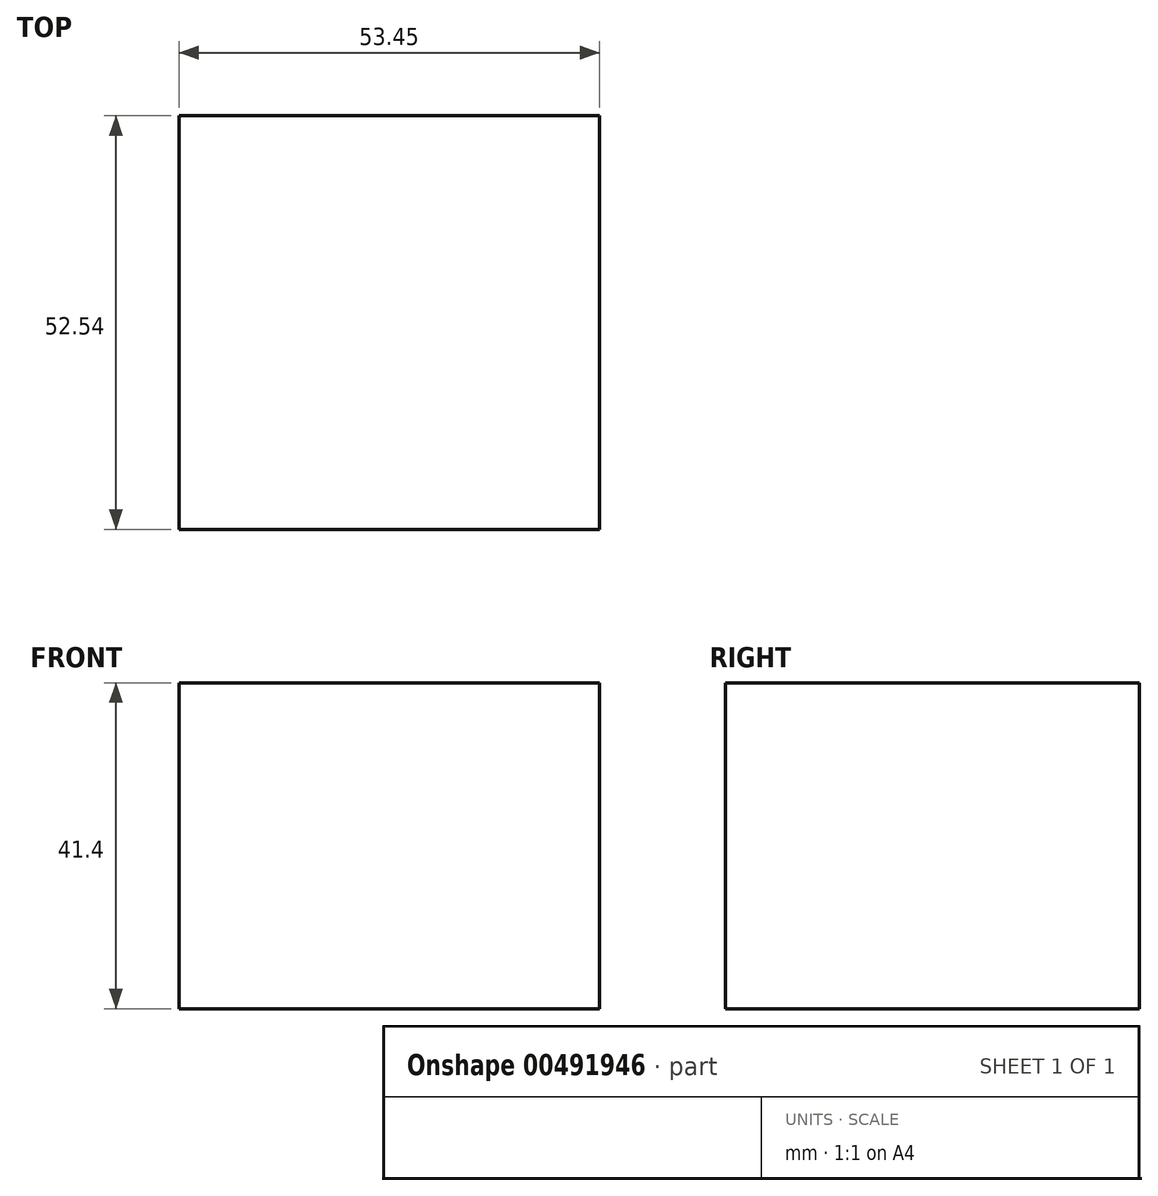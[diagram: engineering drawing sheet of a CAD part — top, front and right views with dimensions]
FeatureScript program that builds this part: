
annotation { "Feature Type Name" : "Feature", "Feature Type Description" : "" }
export const myFeature = defineFeature(function(context is Context, id is Id, definition is map)
    precondition{}
    {
        {
            var Q0;
            Q0=qCreatedBy(makeId("Top.planeOp"),FACE);
            var sketch = newSketch(context, id + "F0", { "sketchPlane" : qUnion([Q0])});
            skLineSegment(sketch, "E0.bottom", {"start": v(0, 0) * mm, "end": v(-53.45, 0) * mm});
            skLineSegment(sketch, "E0.top", {"start": v(0, 52.54) * mm, "end": v(-53.45, 52.54) * mm});
            skLineSegment(sketch, "E0.left", {"start": v(0, 0) * mm, "end": v(0, 52.54) * mm});
            skLineSegment(sketch, "E0.right", {"start": v(-53.45, 0) * mm, "end": v(-53.45, 52.54) * mm});
            skSolve(sketch);
        }
        {
            var Q0;
            Q0=makeQuery(id+"F0.imprint","IMPRINT",FACE,{"disambiguationData":[TD([[makeQuery(id+"F0.imprint","IMPRINT",EDGE,{"derivedFrom":sQuery(id+"F0.wireOp",EDGE,"E0.bottom")}),-1.0]])]});
            extrude(context, id + "F1", {"entities" : qUnion([Q0]), "oppositeDirection" : true, "depth" : 41.4 * mm});
        }
    });
